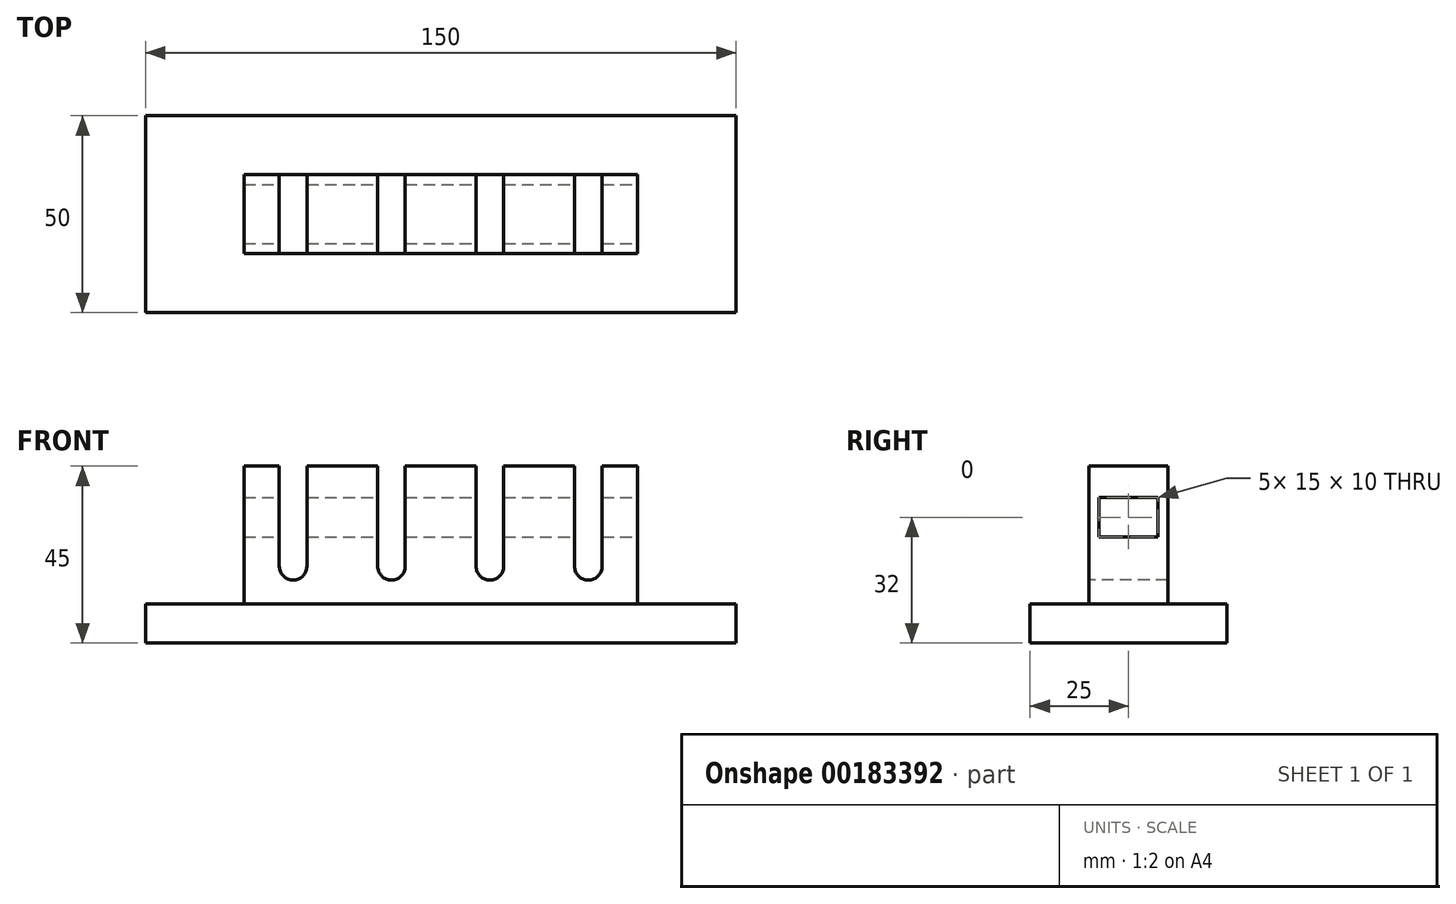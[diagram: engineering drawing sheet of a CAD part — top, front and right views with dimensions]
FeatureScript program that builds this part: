
annotation { "Feature Type Name" : "Feature", "Feature Type Description" : "" }
export const myFeature = defineFeature(function(context is Context, id is Id, definition is map)
    precondition{}
    {
        {
            var Q0;
            Q0=qCreatedBy(makeId("Top.planeOp"),FACE);
            var sketch = newSketch(context, id + "F0", { "sketchPlane" : qUnion([Q0])});
            skLineSegment(sketch, "E0.bottom", {"start": v(0, 0) * mm, "end": v(150, 0) * mm});
            skLineSegment(sketch, "E0.top", {"start": v(0, 50) * mm, "end": v(150, 50) * mm});
            skLineSegment(sketch, "E0.left", {"start": v(0, 0) * mm, "end": v(0, 50) * mm});
            skLineSegment(sketch, "E0.right", {"start": v(150, 0) * mm, "end": v(150, 50) * mm});
            skSolve(sketch);
        }
        {
            var Q0;
            Q0=makeQuery(id+"F0.imprint","IMPRINT",FACE,{"disambiguationData":[TD([[makeQuery(id+"F0.imprint","IMPRINT",EDGE,{"derivedFrom":sQuery(id+"F0.wireOp",EDGE,"E0.bottom")}),1.0]])]});
            extrude(context, id + "F1", {"entities" : qUnion([Q0]), "depth" : 10 * mm});
        }
        {
            var Q0;
            Q0=makeQuery(id+"F1.opExtrude","CAP_FACE",FACE,{"disambiguationData":[OSD([sQuery(id+"F0.wireOp",EDGE,"E0.bottom"),sQuery(id+"F0.wireOp",EDGE,"E0.top"),sQuery(id+"F0.wireOp",EDGE,"E0.left"),sQuery(id+"F0.wireOp",EDGE,"E0.right")])],"isStart":false});
            var sketch = newSketch(context, id + "F2", { "sketchPlane" : qUnion([Q0])});
            skLineSegment(sketch, "E1.bottom", {"start": v(25, 35) * mm, "end": v(125, 35) * mm});
            skLineSegment(sketch, "E1.top", {"start": v(25, 15) * mm, "end": v(125, 15) * mm});
            skLineSegment(sketch, "E1.left", {"start": v(25, 35) * mm, "end": v(25, 15) * mm});
            skLineSegment(sketch, "E1.right", {"start": v(125, 35) * mm, "end": v(125, 15) * mm});
            skSolve(sketch);
        }
        {
            var Q0;
            Q0 = qSketchRegion(id + "F2", true);
            extrude(context, id + "F3", {"entities" : qUnion([Q0]), "operationType" : NewBodyOperationType.ADD, "depth" : 35 * mm});
        }
        {
            var Q0;
            Q0=makeQuery(id+"F3.opExtrude","SWEPT_FACE",FACE,{"disambiguationData":[OSD([sQuery(id+"F2.wireOp",EDGE,"E1.top")])]});
            var sketch = newSketch(context, id + "F4", { "sketchPlane" : qUnion([Q0])});
            skLineSegment(sketch, "E2", {"start": v(34, 45) * mm, "end": v(34, 19.5) * mm});
            skArc(sketch, "E3", {"start": v(34, 19.5) * mm, "mid": v(37.5, 16) * mm, "end": v(41, 19.5) * mm});
            skLineSegment(sketch, "E4", {"start": v(41, 19.5) * mm, "end": v(41, 45) * mm});
            skLineSegment(sketch, "E5", {"start": v(41, 45) * mm, "end": v(34, 45) * mm});
            skLineSegment(sketch, "E6", {"start": v(75, 45) * mm, "end": v(75, 10) * mm, "construction": true});
            skLineSegment(sketch, "E7.MirrorCS", {"start": v(116, 45) * mm, "end": v(116, 19.5) * mm});
            skArc(sketch, "E8.MirrorCS", {"start": v(116, 19.5) * mm, "mid": v(112.5, 16) * mm, "end": v(109, 19.5) * mm});
            skLineSegment(sketch, "E9.MirrorCS", {"start": v(109, 19.5) * mm, "end": v(109, 45) * mm});
            skLineSegment(sketch, "E10.MirrorCS", {"start": v(109, 45) * mm, "end": v(116, 45) * mm});
            skLineSegment(sketch, "E11", {"start": v(50, 45) * mm, "end": v(50, 10) * mm, "construction": true});
            skLineSegment(sketch, "E12.MirrorCS", {"start": v(59, 45) * mm, "end": v(66, 45) * mm});
            skLineSegment(sketch, "E13.MirrorCS", {"start": v(66, 45) * mm, "end": v(66, 19.5) * mm});
            skLineSegment(sketch, "E14.MirrorCS", {"start": v(59, 19.5) * mm, "end": v(59, 45) * mm});
            skArc(sketch, "E15.MirrorCS", {"start": v(66, 19.5) * mm, "mid": v(62.5, 16) * mm, "end": v(59, 19.5) * mm});
            skLineSegment(sketch, "E16.MirrorCS", {"start": v(91, 19.5) * mm, "end": v(91, 45) * mm});
            skLineSegment(sketch, "E17.MirrorCS", {"start": v(91, 45) * mm, "end": v(84, 45) * mm});
            skLineSegment(sketch, "E18.MirrorCS", {"start": v(84, 45) * mm, "end": v(84, 19.5) * mm});
            skArc(sketch, "E19.MirrorCS", {"start": v(84, 19.5) * mm, "mid": v(87.5, 16) * mm, "end": v(91, 19.5) * mm});
            skSolve(sketch);
        }
        {
            var Q0;
            Q0 = qSketchRegion(id + "F4", true);
            extrude(context, id + "F5", {"entities" : qUnion([Q0]), "operationType" : NewBodyOperationType.REMOVE, "endBound" : BoundingType.THROUGH_ALL, "oppositeDirection" : true, "depth" : 25 * mm});
        }
        {
            var Q0;
            Q0=makeQuery(id+"F3.opExtrude","SWEPT_FACE",FACE,{"disambiguationData":[OSD([sQuery(id+"F2.wireOp",EDGE,"E1.right")])]});
            var sketch = newSketch(context, id + "F6", { "sketchPlane" : qUnion([Q0])});
            skLineSegment(sketch, "E20.bottom", {"start": v(17.5, 37) * mm, "end": v(32.5, 37) * mm});
            skLineSegment(sketch, "E20.top", {"start": v(17.5, 27) * mm, "end": v(32.5, 27) * mm});
            skLineSegment(sketch, "E20.left", {"start": v(17.5, 37) * mm, "end": v(17.5, 27) * mm});
            skLineSegment(sketch, "E20.right", {"start": v(32.5, 37) * mm, "end": v(32.5, 27) * mm});
            skSolve(sketch);
        }
        {
            var Q0;
            Q0=makeQuery(id+"F6.imprint","IMPRINT",FACE,{"disambiguationData":[TD([[makeQuery(id+"F6.imprint","IMPRINT",EDGE,{"derivedFrom":sQuery(id+"F6.wireOp",EDGE,"E20.bottom")}),-1.0]])]});
            extrude(context, id + "F7", {"entities" : qUnion([Q0]), "operationType" : NewBodyOperationType.REMOVE, "endBound" : BoundingType.THROUGH_ALL, "oppositeDirection" : true, "depth" : 25 * mm});
        }
    });
